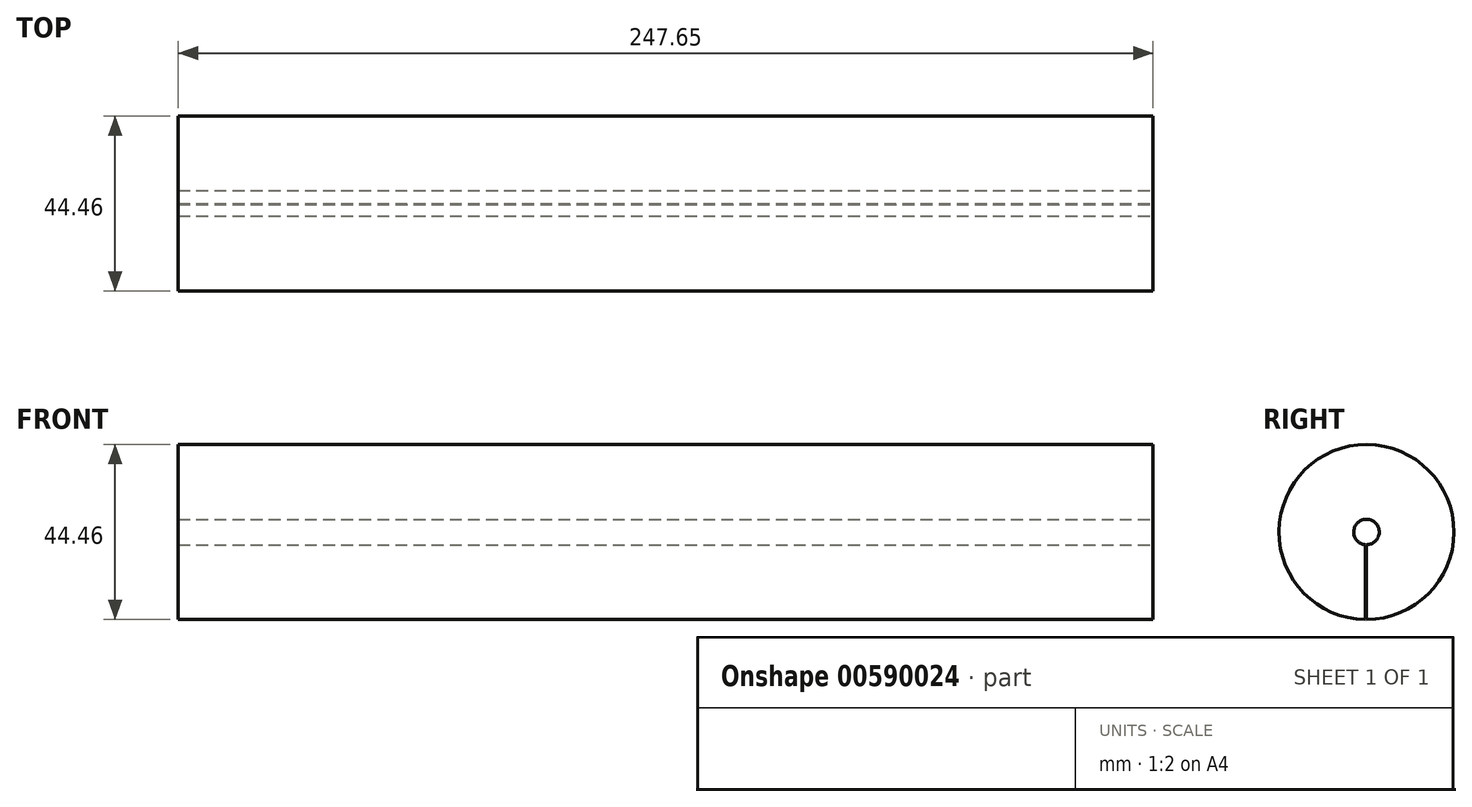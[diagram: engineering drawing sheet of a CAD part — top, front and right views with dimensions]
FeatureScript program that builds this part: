
annotation { "Feature Type Name" : "Feature", "Feature Type Description" : "" }
export const myFeature = defineFeature(function(context is Context, id is Id, definition is map)
    precondition{}
    {
        {
            var Q0;
            Q0=qCreatedBy(makeId("Right.planeOp"),FACE);
            var sketch = newSketch(context, id + "F0", { "sketchPlane" : qUnion([Q0])});
            skCircle(sketch, "E0", {"center": v(0, 0) * mm, "radius": 22.23 * mm});
            skSolve(sketch);
        }
        {
            var Q0;
            Q0=makeQuery(id+"F0.imprint","IMPRINT",FACE,{"disambiguationData":[TD([[makeQuery(id+"F0.imprint","IMPRINT",EDGE,{"derivedFrom":sQuery(id+"F0.wireOp",EDGE,"E0")}),1.0]])]});
            extrude(context, id + "F1", {"entities" : qUnion([Q0]), "depth" : 247.65 * mm, "offsetDistance" : 25.4 * mm});
        }
        {
            var Q0;
            Q0=makeQuery(id+"F1.opExtrude","CAP_FACE",FACE,{"disambiguationData":[OSD([sQuery(id+"F0.wireOp",EDGE,"E0")])],"isStart":false});
            var sketch = newSketch(context, id + "F2", { "sketchPlane" : qUnion([Q0])});
            skCircle(sketch, "E1", {"center": v(0, 0) * mm, "radius": 3.24 * mm});
            skSolve(sketch);
        }
        {
            var Q0;
            Q0=makeQuery(id+"F2.imprint","IMPRINT",FACE,{"disambiguationData":[TD([[makeQuery(id+"F2.imprint","IMPRINT",EDGE,{"derivedFrom":sQuery(id+"F2.wireOp",EDGE,"E1")}),1.0]])]});
            extrude(context, id + "F3", {"entities" : qUnion([Q0]), "operationType" : NewBodyOperationType.REMOVE, "oppositeDirection" : true, "depth" : 304.8 * mm, "offsetDistance" : 25.4 * mm});
        }
        {
            var Q0;
            Q0=makeQuery(id+"F1.opExtrude","CAP_FACE",FACE,{"disambiguationData":[OSD([sQuery(id+"F0.wireOp",EDGE,"E0")])],"isStart":false});
            var sketch = newSketch(context, id + "F4", { "sketchPlane" : qUnion([Q0])});
            skLineSegment(sketch, "E2.bottom", {"start": v(0, -22.23) * mm, "end": v(-0.25, -22.23) * mm});
            skLineSegment(sketch, "E2.top", {"start": v(0, 0) * mm, "end": v(-0.25, 0) * mm});
            skLineSegment(sketch, "E2.left", {"start": v(0, -22.23) * mm, "end": v(0, 0) * mm});
            skLineSegment(sketch, "E2.right", {"start": v(-0.25, -22.23) * mm, "end": v(-0.25, 0) * mm});
            skSolve(sketch);
        }
        {
            var Q0;
            Q0=qSketchRegion(id+"F4",true);
            extrude(context, id + "F5", {"entities" : qUnion([Q0]), "operationType" : NewBodyOperationType.REMOVE, "oppositeDirection" : true, "depth" : 304.8 * mm, "offsetDistance" : 25.4 * mm});
        }
    });
